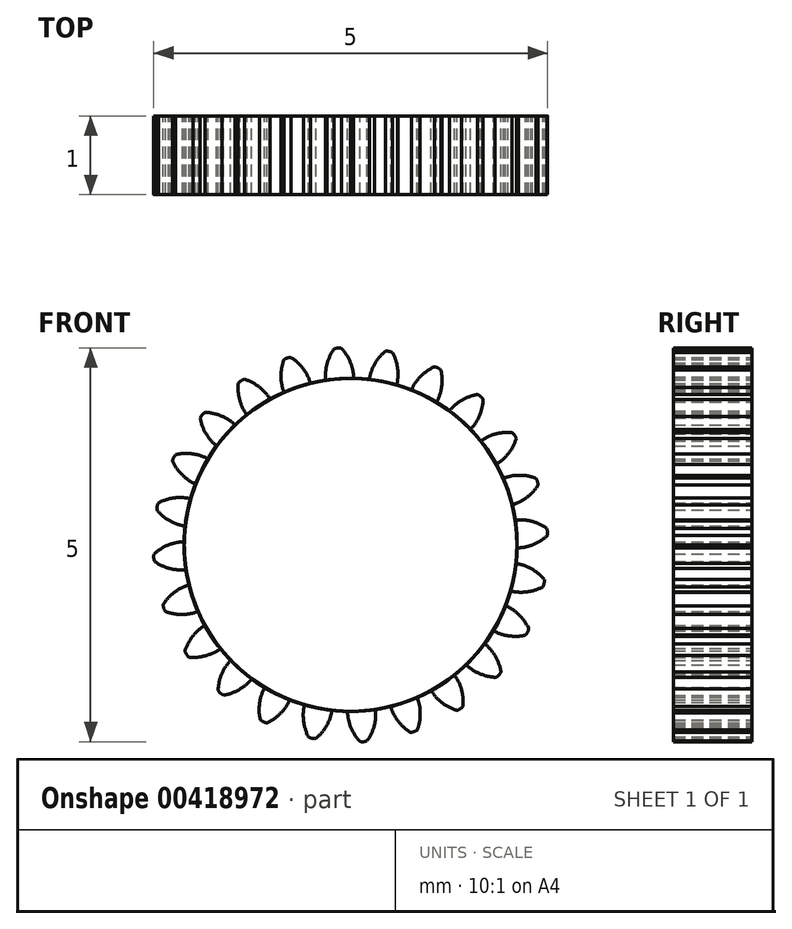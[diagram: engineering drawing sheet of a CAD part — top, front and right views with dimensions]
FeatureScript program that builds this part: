
annotation { "Feature Type Name" : "Feature", "Feature Type Description" : "" }
export const myFeature = defineFeature(function(context is Context, id is Id, definition is map)
    precondition{}
    {
        {
            var Q0;
            Q0=qCreatedBy(makeId("Front.planeOp"),FACE);
            var sketch = newSketch(context, id + "F0", { "sketchPlane" : qUnion([Q0])});
            skCircle(sketch, "E0", {"center": v(0, 0) * mm, "radius": 2.12 * mm});
            skCircle(sketch, "E1", {"center": v(0, 0) * mm, "radius": 2.31 * mm, "construction": true});
            skCircle(sketch, "E2", {"center": v(0, 0) * mm, "radius": 2.5 * mm, "construction": true});
            skLineSegment(sketch, "E3", {"start": v(0, 0) * mm, "end": v(0, 3.11) * mm, "construction": true});
            skLineSegment(sketch, "E4", {"start": v(0, 0) * mm, "end": v(-0.21, 3.21) * mm, "construction": true});
            skLineSegment(sketch, "E5", {"start": v(0, 2.31) * mm, "end": v(-1.93, 2.31) * mm, "construction": true});
            skLineSegment(sketch, "E6", {"start": v(0, 2.31) * mm, "end": v(-2.47, 1.41) * mm, "construction": true});
            skCircle(sketch, "E7", {"center": v(0, 2.31) * mm, "radius": 0.57 * mm, "construction": true});
            skCircle(sketch, "E8", {"center": v(0, 0) * mm, "radius": 2.17 * mm, "construction": true});
            skCircle(sketch, "E9", {"center": v(-0.54, 2.1) * mm, "radius": 0.57 * mm, "construction": true});
            skArc(sketch, "E10", {"start": v(0, 2.31) * mm, "mid": v(-0.05, 2.4) * mm, "end": v(-0.12, 2.5) * mm});
            skArc(sketch, "E11", {"start": v(0.04, 2.11) * mm, "mid": v(0.03, 2.21) * mm, "end": v(0, 2.31) * mm});
            skArc(sketch, "E12.MirrorCS", {"start": v(-0.3, 2.3) * mm, "mid": v(-0.27, 2.4) * mm, "end": v(-0.2, 2.5) * mm});
            skArc(sketch, "E13.MirrorCS", {"start": v(-0.31, 2.1) * mm, "mid": v(-0.32, 2.2) * mm, "end": v(-0.3, 2.3) * mm});
            skArc(sketch, "E14", {"start": v(-0.12, 2.5) * mm, "mid": v(-0.16, 2.5) * mm, "end": v(-0.2, 2.5) * mm});
            skSolve(sketch);
        }
        {
            var Q0;
            Q0=makeQuery(id+"F0.imprint","IMPRINT",FACE,{"disambiguationData":[TD([[makeQuery(id+"F0.imprint","IMPRINT",EDGE,{"derivedFrom":sQuery(id+"F0.wireOp",EDGE,"E10")}),1.0]])]});
            var Q1;
            {var subQ0=sQuery(id+"F0.wireOp",EDGE,"E0");var subQ1=makeQuery(id+"F0.imprint","INTERSECT",VERTEX,{"derivedFrom":[subQ0,sQuery(id+"F0.wireOp",EDGE,"E11")]});Q1=makeQuery(id+"F0.imprint","IMPRINT",FACE,{"disambiguationData":[TD([[makeQuery(id+"F0.imprint","IMPRINT",EDGE,{"disambiguationData":[TD([[subQ1,-1.0]])],"derivedFrom":subQ0}),1.0]])]});}
            extrude(context, id + "F1", {"entities" : qUnion([Q0, Q1]), "depth" : 1 * mm});
        }
        {
            var Q0;
            Q0=makeQuery(id+"F1.opExtrude","SWEPT_BODY",BODY,{"disambiguationData":[OSD([sQuery(id+"F0.wireOp",EDGE,"E0"),sQuery(id+"F0.wireOp",EDGE,"E10"),sQuery(id+"F0.wireOp",EDGE,"E11"),sQuery(id+"F0.wireOp",EDGE,"E12.MirrorCS"),sQuery(id+"F0.wireOp",EDGE,"E13.MirrorCS"),sQuery(id+"F0.wireOp",EDGE,"E14")])]});
            var Q1;
            Q1=makeQuery(id+"F1.opExtrude","SWEPT_FACE",FACE,{"disambiguationData":[OSD([sQuery(id+"F0.wireOp",EDGE,"E0")])]});
            circularPattern(context, id + "F2", {"entities" : qUnion([Q0]), "axis" : qUnion([Q1]), "angle" : 360 * degree, "instanceCount" : 24, "equalSpace" : true});
        }
    });
